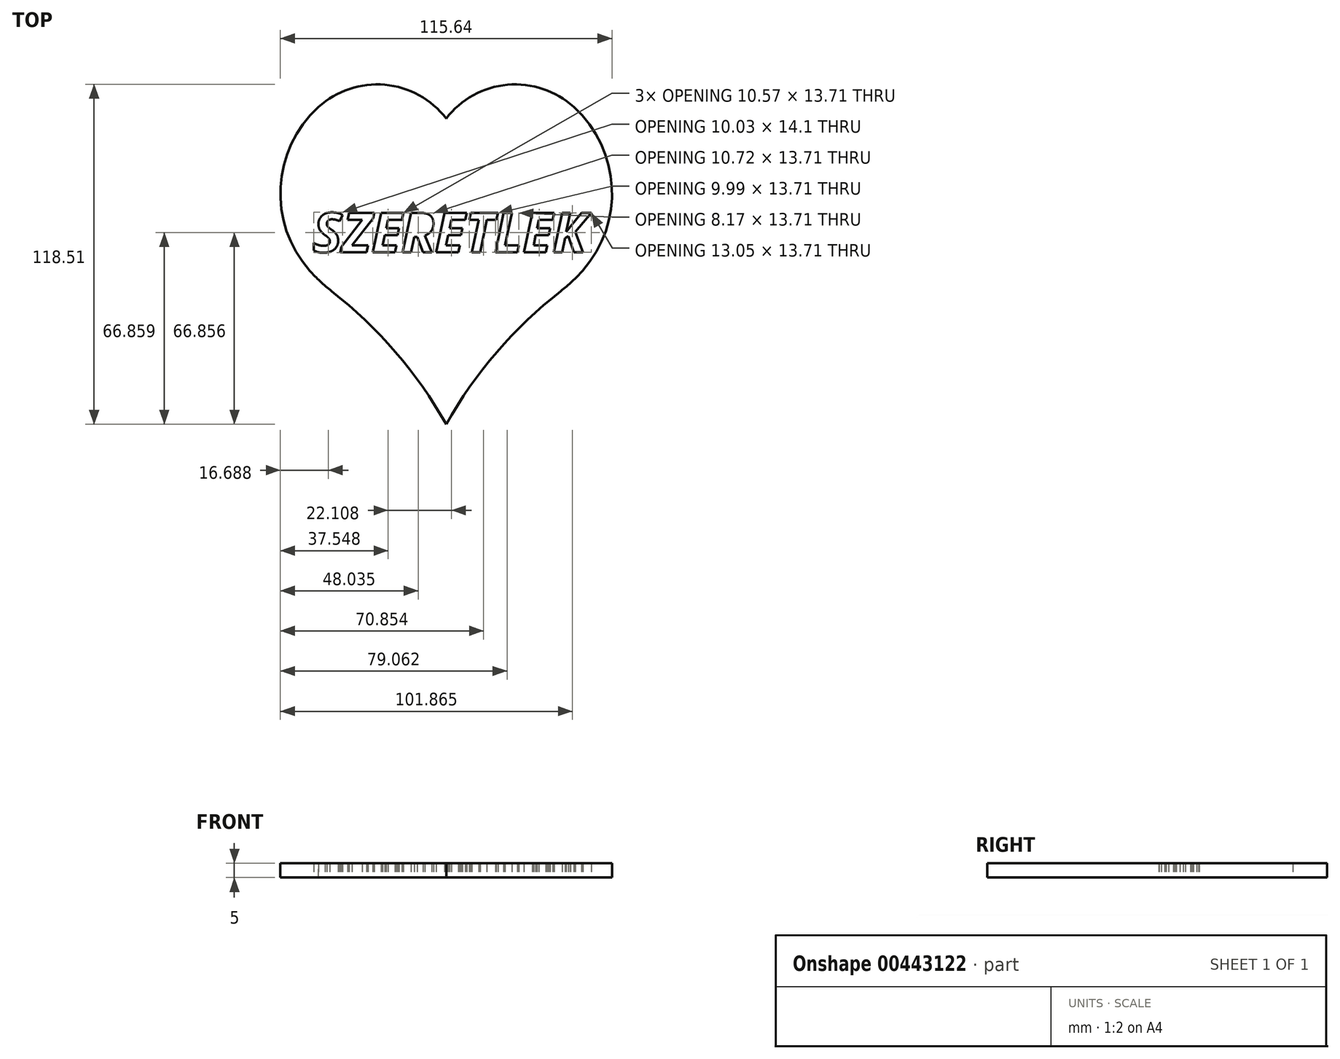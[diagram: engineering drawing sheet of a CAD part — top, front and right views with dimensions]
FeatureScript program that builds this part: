
annotation { "Feature Type Name" : "Feature", "Feature Type Description" : "" }
export const myFeature = defineFeature(function(context is Context, id is Id, definition is map)
    precondition{}
    {
        {
            var Q0;
            Q0=qCreatedBy(makeId("Top.planeOp"),FACE);
            var sketch = newSketch(context, id + "F0", { "sketchPlane" : qUnion([Q0])});
            skPoint(sketch, "E0.middle", {"position": v(0, 0) * mm});
            skArc(sketch, "E1", {"start": v(47.56, -6.45) * mm, "mid": v(57.76, 22.73) * mm, "end": v(44.48, 50.63) * mm});
            skArc(sketch, "E2", {"start": v(44.48, 50.63) * mm, "mid": v(21.36, 58.38) * mm, "end": v(0, 46.6) * mm});
            skPoint(sketch, "E3.start.orphan", {"position": v(0, -60) * mm});
            skArc(sketch, "E4", {"start": v(47.56, -6.45) * mm, "mid": v(43.94, -10.17) * mm, "end": v(39.98, -13.55) * mm});
            skArc(sketch, "E5", {"start": v(39.98, -13.55) * mm, "mid": v(17.68, -34.79) * mm, "end": v(0, -60) * mm});
            skArc(sketch, "E6.MirrorCS", {"start": v(-44.48, 50.63) * mm, "mid": v(-21.36, 58.38) * mm, "end": v(0, 46.6) * mm});
            skArc(sketch, "E7.MirrorCS", {"start": v(-47.56, -6.45) * mm, "mid": v(-57.76, 22.73) * mm, "end": v(-44.48, 50.63) * mm});
            skArc(sketch, "E8.MirrorCS", {"start": v(-47.56, -6.45) * mm, "mid": v(-43.94, -10.17) * mm, "end": v(-39.98, -13.55) * mm});
            skArc(sketch, "E9.MirrorCS", {"start": v(-39.98, -13.55) * mm, "mid": v(-17.68, -34.79) * mm, "end": v(0, -60) * mm});
            skPoint(sketch, "E0.top.end.orphan", {"position": v(-60, 60) * mm});
            skPoint(sketch, "E0.left.end.orphan", {"position": v(60, 60) * mm});
            skPoint(sketch, "E10.orphan", {"position": v(60, -60) * mm});
            skPoint(sketch, "E0.bottom.end.orphan", {"position": v(-60, -60) * mm});
            skText(sketch, "E11", { "text": "SZERETLEK", "fontName": "OpenSans-BoldItalic.ttf"});
            const initialGuessF0  = {"E11": [-0.04653, 0, 1, 0, 0.01383]};
            skSetInitialGuess(sketch, initialGuessF0);
            skSolve(sketch);
        }
        {
            var Q0;
            Q0=makeQuery(id+"F0.imprint","IMPRINT",FACE,{"disambiguationData":[TD([[makeQuery(id+"F0.imprint","IMPRINT",EDGE,{"derivedFrom":sQuery(id+"F0.wireOp",EDGE,"E1")}),1.0]])]});
            extrude(context, id + "F1", {"entities" : qUnion([Q0]), "depth" : 5 * mm});
        }
    });
